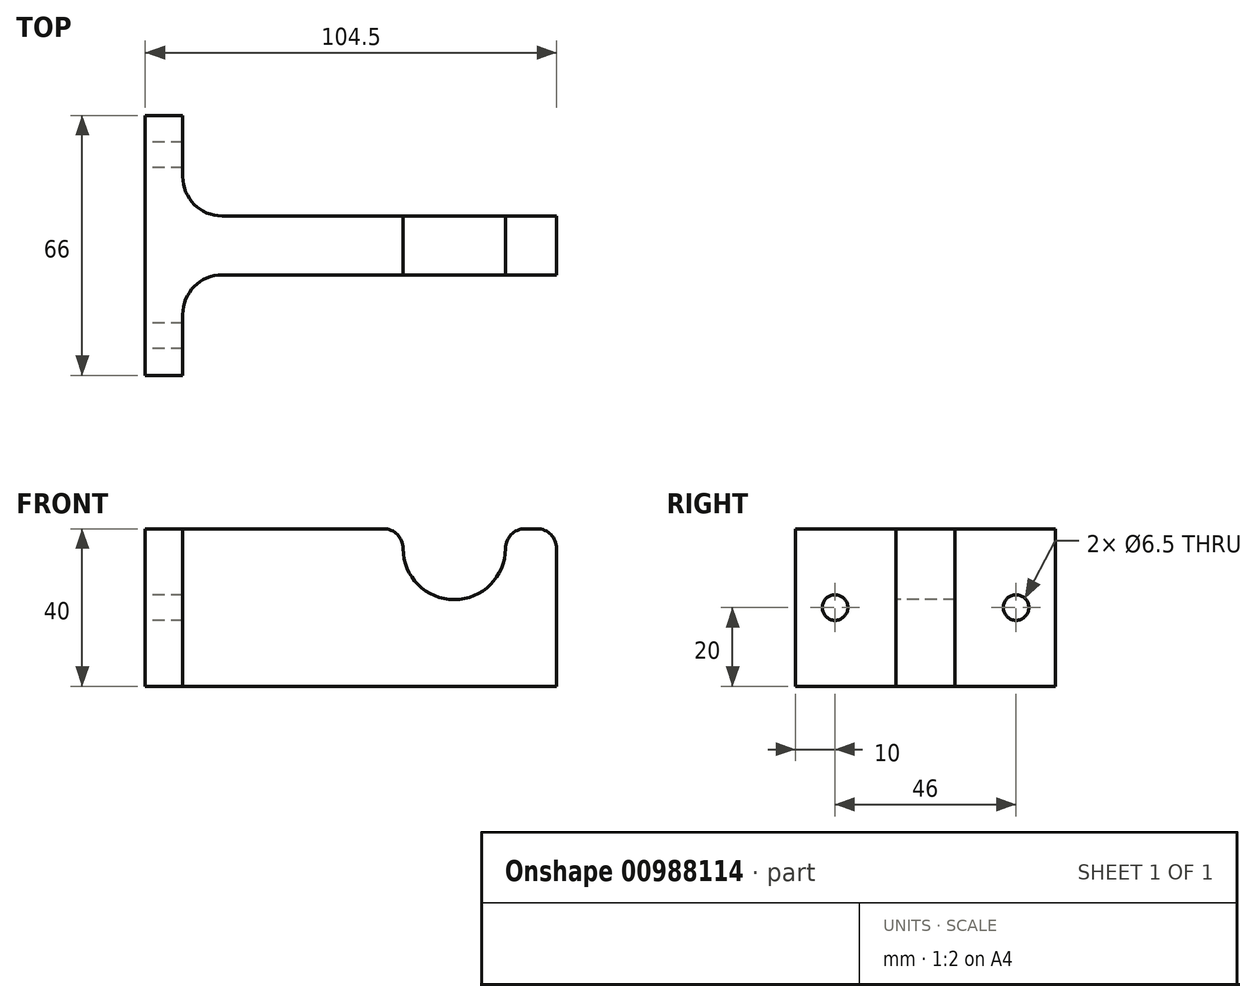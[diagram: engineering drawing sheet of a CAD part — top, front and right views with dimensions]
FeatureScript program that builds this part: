
annotation { "Feature Type Name" : "Feature", "Feature Type Description" : "" }
export const myFeature = defineFeature(function(context is Context, id is Id, definition is map)
    precondition{}
    {
        {
            var Q0;
            Q0=qCreatedBy(makeId("Top.planeOp"),FACE);
            var sketch = newSketch(context, id + "F0", { "sketchPlane" : qUnion([Q0])});
            skLineSegment(sketch, "E0", {"start": v(0, 0) * mm, "end": v(0, 66) * mm});
            skLineSegment(sketch, "E1", {"start": v(0, 66) * mm, "end": v(9.5, 66) * mm});
            skLineSegment(sketch, "E2", {"start": v(9.5, 66) * mm, "end": v(9.5, 40.5) * mm});
            skLineSegment(sketch, "E3", {"start": v(9.5, 40.5) * mm, "end": v(104.5, 40.5) * mm});
            skLineSegment(sketch, "E4", {"start": v(104.5, 40.5) * mm, "end": v(104.5, 25.5) * mm});
            skLineSegment(sketch, "E5", {"start": v(104.5, 25.5) * mm, "end": v(9.5, 25.5) * mm});
            skLineSegment(sketch, "E6", {"start": v(9.5, 25.5) * mm, "end": v(9.5, 0) * mm});
            skLineSegment(sketch, "E7", {"start": v(9.5, 0) * mm, "end": v(0, 0) * mm});
            skLineSegment(sketch, "E8", {"start": v(46.19, 33) * mm, "end": v(-23.48, 33) * mm, "construction": true});
            skPoint(sketch, "E8.startSnap0", {"position": v(0, 33) * mm});
            skSolve(sketch);
        }
        {
            var Q0;
            Q0 = qSketchRegion(id + "F0", true);
            extrude(context, id + "F1", {"entities" : qUnion([Q0]), "depth" : 40 * mm, "offsetDistance" : 25 * mm});
        }
        {
            var Q0;
            Q0=makeQuery(id+"F1.opExtrude","SWEPT_FACE",FACE,{"disambiguationData":[OSD([sQuery(id+"F0.wireOp",EDGE,"E0")])]});
            var sketch = newSketch(context, id + "F2", { "sketchPlane" : qUnion([Q0])});
            skLineSegment(sketch, "E9", {"start": v(-66, 20) * mm, "end": v(0, 20) * mm, "construction": true});
            skLineSegment(sketch, "E10", {"start": v(-33, 40) * mm, "end": v(-33, 0) * mm, "construction": true});
            skCircle(sketch, "E11", {"center": v(-56, 20) * mm, "radius": 3.25 * mm});
            skCircle(sketch, "E12", {"center": v(-10, 20) * mm, "radius": 3.25 * mm});
            skSolve(sketch);
        }
        {
            var Q0;
            Q0 = qSketchRegion(id + "F2", true);
            extrude(context, id + "F3", {"entities" : qUnion([Q0]), "operationType" : NewBodyOperationType.REMOVE, "endBound" : BoundingType.THROUGH_ALL, "oppositeDirection" : true, "depth" : 25 * mm, "offsetDistance" : 25 * mm});
        }
        {
            var Q0;
            Q0=makeQuery(id+"F1.opExtrude","SWEPT_FACE",FACE,{"disambiguationData":[OSD([sQuery(id+"F0.wireOp",EDGE,"E5")])]});
            var sketch = newSketch(context, id + "F4", { "sketchPlane" : qUnion([Q0])});
            skCircle(sketch, "E13", {"center": v(78.5, 35) * mm, "radius": 13 * mm});
            skLineSegment(sketch, "E14.bottom", {"start": v(91.5, 35) * mm, "end": v(65.5, 35) * mm});
            skLineSegment(sketch, "E14.top", {"start": v(91.5, 50.46) * mm, "end": v(65.5, 50.46) * mm});
            skLineSegment(sketch, "E14.left", {"start": v(91.5, 35) * mm, "end": v(91.5, 50.46) * mm});
            skLineSegment(sketch, "E14.right", {"start": v(65.5, 35) * mm, "end": v(65.5, 50.46) * mm});
            skSolve(sketch);
        }
        {
            var Q0;
            Q0 = qSketchRegion(id + "F4", true);
            extrude(context, id + "F5", {"entities" : qUnion([Q0]), "operationType" : NewBodyOperationType.REMOVE, "endBound" : BoundingType.THROUGH_ALL, "oppositeDirection" : true, "depth" : 25 * mm, "offsetDistance" : 25 * mm});
        }
        {
            var Q0;
            Q0=makeQuery(id+"F1.opExtrude","SWEPT_EDGE",EDGE,{"disambiguationData":[OSD([sQuery(id+"F0.wireOp",EDGE,"E5"),sQuery(id+"F0.wireOp",EDGE,"E6")])]});
            var Q1;
            Q1=makeQuery(id+"F1.opExtrude","SWEPT_EDGE",EDGE,{"disambiguationData":[OSD([sQuery(id+"F0.wireOp",EDGE,"E2"),sQuery(id+"F0.wireOp",EDGE,"E3")])]});
            fillet(context, id + "F6", {"entities" : qUnion([Q0, Q1]), "tangentPropagation" : true, "radius" : 10 * mm, "defaultsChanged" : true, "vertexSettings" : [], "allowEdgeOverflow" : false});
        }
        {
            var Q0;
            Q0=makeQuery(id+"F5.boolean.opBoolean","INTERSECT",EDGE,{"derivedFrom":[makeQuery(id+"F1.opExtrude","CAP_FACE",FACE,{"disambiguationData":[OSD([sQuery(id+"F0.wireOp",EDGE,"E0"),sQuery(id+"F0.wireOp",EDGE,"E1"),sQuery(id+"F0.wireOp",EDGE,"E2"),sQuery(id+"F0.wireOp",EDGE,"E3"),sQuery(id+"F0.wireOp",EDGE,"E4"),sQuery(id+"F0.wireOp",EDGE,"E5"),sQuery(id+"F0.wireOp",EDGE,"E6"),sQuery(id+"F0.wireOp",EDGE,"E7")])],"isStart":false}),makeQuery(id+"F5.opExtrude","SWEPT_FACE",FACE,{"disambiguationData":[OSD([sQuery(id+"F4.wireOp",EDGE,"E14.right")])]})]});
            var Q1;
            Q1=makeQuery(id+"F5.boolean.opBoolean","INTERSECT",EDGE,{"derivedFrom":[makeQuery(id+"F1.opExtrude","CAP_FACE",FACE,{"disambiguationData":[OSD([sQuery(id+"F0.wireOp",EDGE,"E0"),sQuery(id+"F0.wireOp",EDGE,"E1"),sQuery(id+"F0.wireOp",EDGE,"E2"),sQuery(id+"F0.wireOp",EDGE,"E3"),sQuery(id+"F0.wireOp",EDGE,"E4"),sQuery(id+"F0.wireOp",EDGE,"E5"),sQuery(id+"F0.wireOp",EDGE,"E6"),sQuery(id+"F0.wireOp",EDGE,"E7")])],"isStart":false}),makeQuery(id+"F5.opExtrude","SWEPT_FACE",FACE,{"disambiguationData":[OSD([sQuery(id+"F4.wireOp",EDGE,"E14.left")])]})]});
            fillet(context, id + "F7", {"entities" : qUnion([Q0, Q1]), "tangentPropagation" : true, "radius" : 5 * mm, "defaultsChanged" : false, "vertexSettings" : [], "allowEdgeOverflow" : false});
        }
        {
            var Q0;
            Q0=makeQuery(id+"F1.opExtrude","CAP_EDGE",EDGE,{"disambiguationData":[OSD([sQuery(id+"F0.wireOp",EDGE,"E4")])],"isStart":false});
            fillet(context, id + "F8", {"entities" : qUnion([Q0]), "tangentPropagation" : true, "radius" : 5 * mm, "defaultsChanged" : false, "vertexSettings" : [], "allowEdgeOverflow" : false});
        }
    });
